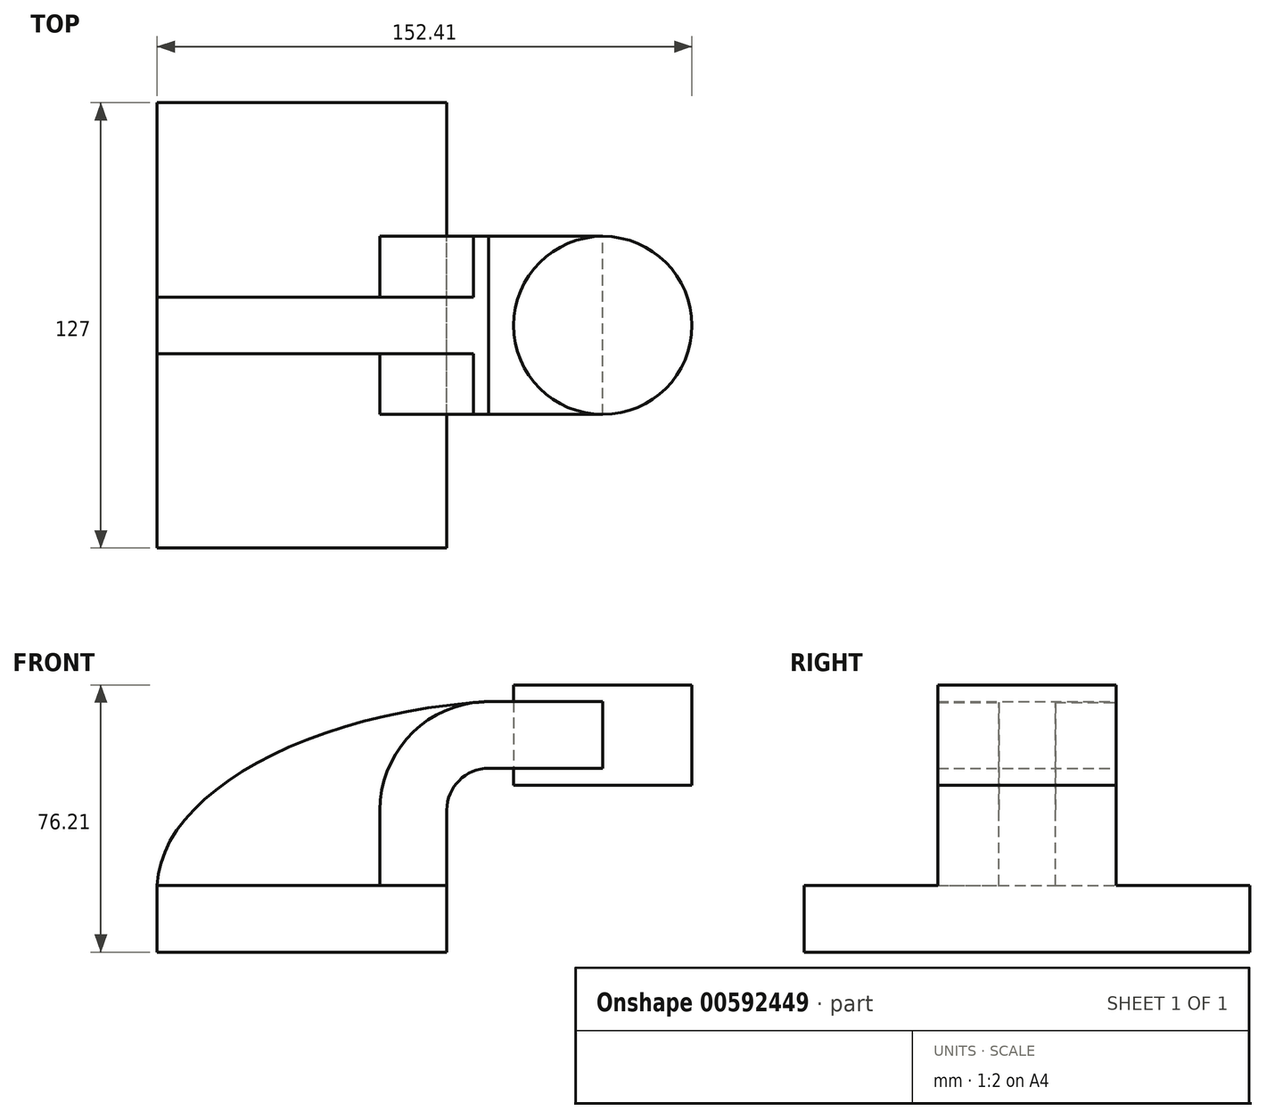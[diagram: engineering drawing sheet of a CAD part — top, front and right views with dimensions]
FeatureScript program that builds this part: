
annotation { "Feature Type Name" : "Feature", "Feature Type Description" : "" }
export const myFeature = defineFeature(function(context is Context, id is Id, definition is map)
    precondition{}
    {
        {
            var Q0;
            Q0=qCreatedBy(makeId("Front.planeOp"),FACE);
            var sketch = newSketch(context, id + "F0", { "sketchPlane" : qUnion([Q0])});
            skLineSegment(sketch, "E0.bottom", {"start": v(41.27, 9.53) * mm, "end": v(-41.28, 9.53) * mm});
            skLineSegment(sketch, "E0.top", {"start": v(41.28, -9.52) * mm, "end": v(-41.27, -9.52) * mm});
            skLineSegment(sketch, "E0.left", {"start": v(41.28, 9.53) * mm, "end": v(41.28, -9.52) * mm});
            skLineSegment(sketch, "E0.right", {"start": v(-41.28, 9.53) * mm, "end": v(-41.27, -9.52) * mm});
            skPoint(sketch, "E0.middle", {"position": v(0, 0) * mm});
            skLineSegment(sketch, "E1.bottom", {"start": v(111.12, 38.1) * mm, "end": v(60.32, 38.1) * mm});
            skLineSegment(sketch, "E1.top", {"start": v(111.12, 66.68) * mm, "end": v(60.32, 66.68) * mm});
            skLineSegment(sketch, "E1.left", {"start": v(111.12, 38.1) * mm, "end": v(111.12, 66.68) * mm});
            skLineSegment(sketch, "E1.right", {"start": v(60.32, 38.1) * mm, "end": v(60.32, 66.68) * mm});
            skPoint(sketch, "E1.middle", {"position": v(85.72, 52.39) * mm});
            skLineSegment(sketch, "E2", {"start": v(41.27, 9.53) * mm, "end": v(41.27, 30.92) * mm});
            skArc(sketch, "E3", {"start": v(41.27, 30.92) * mm, "mid": v(44.78, 39.37) * mm, "end": v(53.23, 42.88) * mm});
            skLineSegment(sketch, "E4", {"start": v(53.23, 42.88) * mm, "end": v(85.72, 42.88) * mm});
            skPoint(sketch, "E4.endSnap0", {"position": v(85.72, 38.1) * mm});
            skArc(sketch, "E5.0", {"start": v(22.22, 30.92) * mm, "mid": v(31.28, 52.82) * mm, "end": v(53.15, 61.93) * mm});
            skLineSegment(sketch, "E5.1", {"start": v(22.22, 9.53) * mm, "end": v(22.22, 30.92) * mm});
            skLineSegment(sketch, "E6", {"start": v(53.15, 61.93) * mm, "end": v(85.72, 61.93) * mm});
            skFitSpline(sketch, "E7", {"points": [v(-41.28, 9.53) * mm, v(53.15, 61.93) * mm], "startDerivative": vector(2.62, 75.57) * mm, "endDerivative": vector(159.45, 9.66) * mm});
            skLineSegment(sketch, "E8", {"start": v(85.72, 38.1) * mm, "end": v(85.72, 66.68) * mm});
            skSolve(sketch);
        }
        {
            var Q0;
            Q0=makeQuery(id+"F0.imprint","IMPRINT",FACE,{"disambiguationData":[TD([[makeQuery(id+"F0.imprint","IMPRINT",EDGE,{"derivedFrom":sQuery(id+"F0.wireOp",EDGE,"E0.top")}),-1.0]])]});
            extrude(context, id + "F1", {"entities" : qUnion([Q0]), "endBound" : BoundingType.SYMMETRIC, "depth" : 127 * mm, "offsetDistance" : 25.4 * mm});
        }
        {
            var Q0;
            {var subQ3=sQuery(id+"F0.wireOp",EDGE,"E5.1");Q0=makeQuery(id+"F0.imprint","IMPRINT",FACE,{"disambiguationData":[TD([[makeQuery(id+"F0.imprint","IMPRINT",EDGE,{"derivedFrom":subQ3}),1.0]])]});}
            extrude(context, id + "F2", {"entities" : qUnion([Q0]), "operationType" : NewBodyOperationType.ADD, "endBound" : BoundingType.SYMMETRIC, "depth" : 16.13 * mm, "offsetDistance" : 25.4 * mm});
        }
        {
            var Q0;
            {var subQ1=sQuery(id+"F0.wireOp",EDGE,"E2");Q0=makeQuery(id+"F0.imprint","IMPRINT",FACE,{"disambiguationData":[TD([[makeQuery(id+"F0.imprint","IMPRINT",EDGE,{"derivedFrom":subQ1}),1.0]])]});}
            var Q1;
            {var subQ0=sQuery(id+"F0.wireOp",EDGE,"E4");var subQ1=sQuery(id+"F0.wireOp",EDGE,"E1.right");var subQ2=makeQuery(id+"F0.imprint","INTERSECT",VERTEX,{"derivedFrom":[subQ1,subQ0]});Q1=makeQuery(id+"F0.imprint","IMPRINT",FACE,{"disambiguationData":[TD([[makeQuery(id+"F0.imprint","IMPRINT",EDGE,{"disambiguationData":[TD([[subQ2,-1.0]])],"derivedFrom":subQ1}),-1.0]])]});}
            extrude(context, id + "F3", {"entities" : qUnion([Q0, Q1]), "operationType" : NewBodyOperationType.ADD, "endBound" : BoundingType.SYMMETRIC, "depth" : 50.8 * mm, "offsetDistance" : 25.4 * mm});
        }
        {
            var Q0;
            {var subQ4=sQuery(id+"F0.wireOp",EDGE,"E1.left");Q0=makeQuery(id+"F0.imprint","IMPRINT",FACE,{"disambiguationData":[TD([[makeQuery(id+"F0.imprint","IMPRINT",EDGE,{"derivedFrom":subQ4}),1.0]])]});}
            var Q1;
            Q1=sQuery(id+"F0.wireOp",EDGE,"E8");
            revolve(context, id + "F4", {"entities" : qUnion([Q0]), "axis" : qUnion([Q1]), "revolveType" : RevolveType.FULL});
        }
    });
